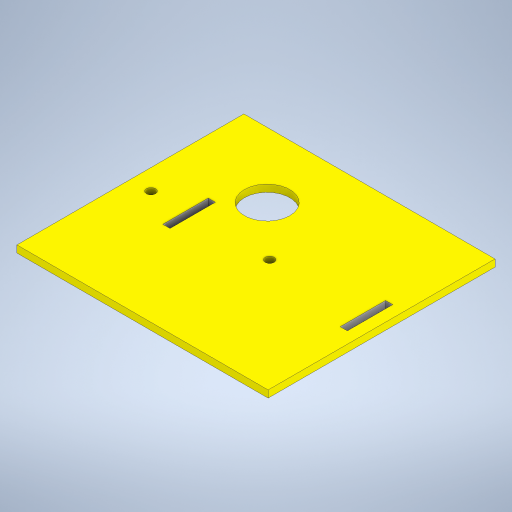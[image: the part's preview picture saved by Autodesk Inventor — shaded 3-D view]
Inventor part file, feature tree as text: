
AUTODESK INVENTOR PART (.ipt)
format: ipt  version: 2024 (Build 280153000, 153)  size: 276,480 bytes
history: native  units: mm
features: extrude x6, sketch x6
ambient origin geometry x8: Origin, YZ Plane, XZ Plane, XY Plane, X Axis, Y Axis, Z Axis, Center Point
bodies: Solid1 (feature_tree)
feature tree (12):
  extrude  "Extrusion1"  Depth=100.0mm
  extrude  "Extrusion9"  Depth=20.0mm
  extrude  "Extrusion10"  Depth=10.0mm
  extrude  "Extrusion11"  Depth=4.0mm
  extrude  "Extrusion14"  Depth=3.155mm
  extrude  "Extrusion15"  Depth=3.155mm
  sketch  "Sketch1"  dims[d0=140.0mm d1=100.0mm]
  sketch  "Sketch9"  dims[d2=3.125mm d3=0.0mm d41=20.0mm]
  sketch  "Sketch10"  dims[d42=10.0mm d43=0.0mm d44=4.0mm]
  sketch  "Sketch11"  dims[d45=5.0mm d46=0.0mm d47=4.0mm]
  sketch  "Sketch15"  dims[d48=5.0mm d49=0.0mm d68=3.155mm]
  sketch  "Sketch16"  dims[d69=20.0mm d70=3.155mm d71=20.0mm d72=75.0mm d73=3.125mm d74=0.0mm d75=3.125mm d76=0.0mm]
